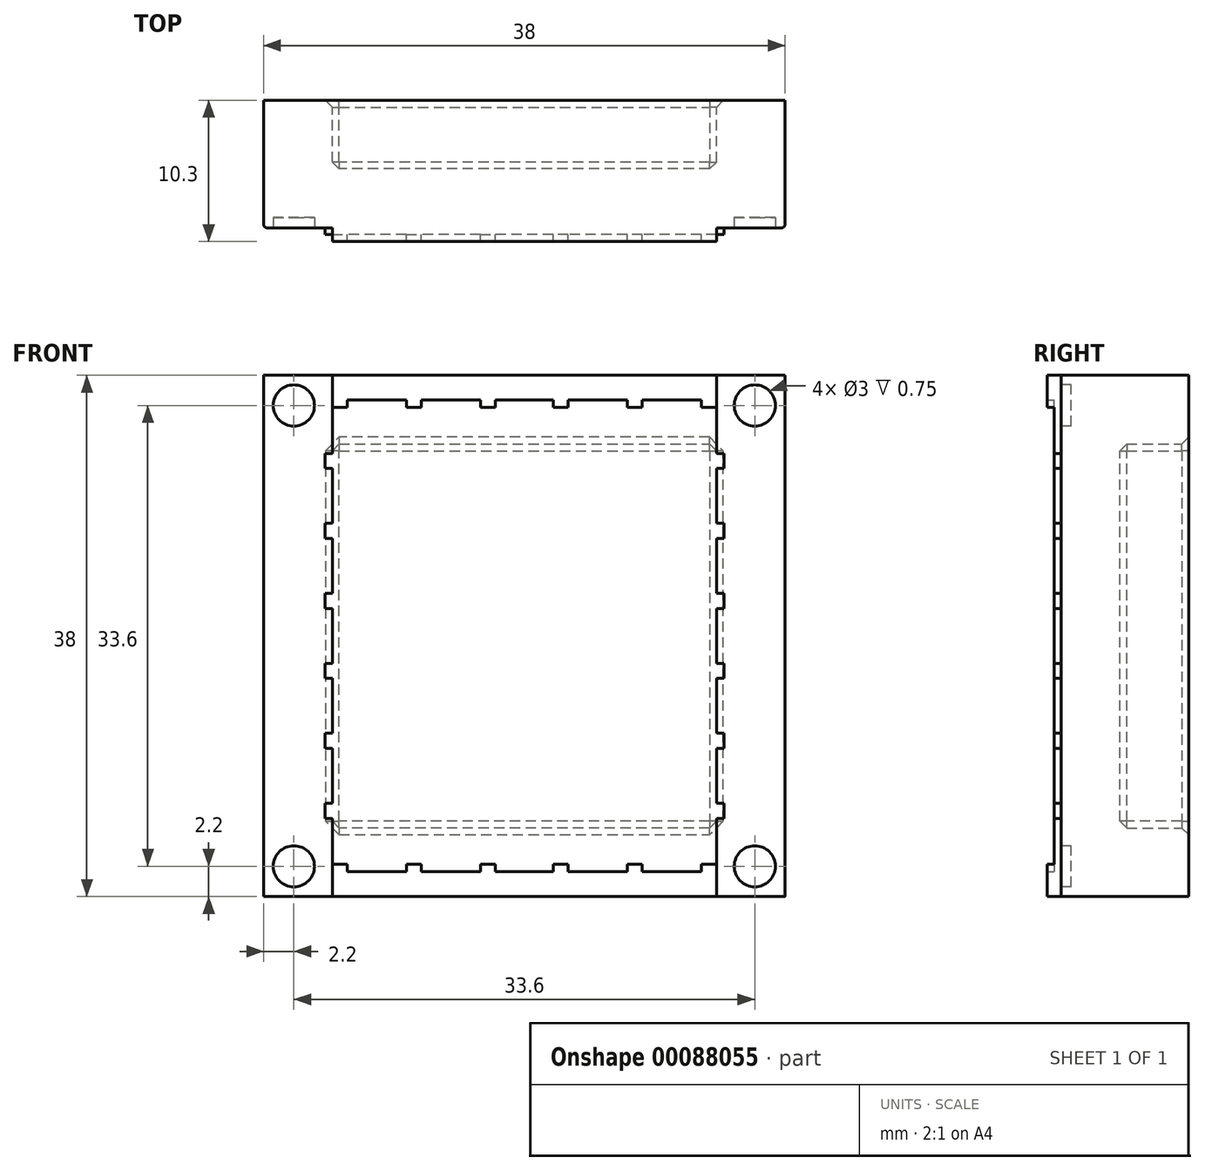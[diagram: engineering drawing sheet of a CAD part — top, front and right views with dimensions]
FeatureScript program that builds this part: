
annotation { "Feature Type Name" : "Feature", "Feature Type Description" : "" }
export const myFeature = defineFeature(function(context is Context, id is Id, definition is map)
    precondition{}
    {
        {
            var Q0;
            Q0=qCreatedBy(makeId("Front.planeOp"),FACE);
            var sketch = newSketch(context, id + "F0", { "sketchPlane" : qUnion([Q0])});
            skLineSegment(sketch, "E0.bottom", {"start": v(-19, 19) * mm, "end": v(19, 19) * mm});
            skLineSegment(sketch, "E0.top", {"start": v(-19, -19) * mm, "end": v(19, -19) * mm});
            skLineSegment(sketch, "E0.left", {"start": v(-19, 19) * mm, "end": v(-19, -19) * mm});
            skLineSegment(sketch, "E0.right", {"start": v(19, 19) * mm, "end": v(19, -19) * mm});
            skPoint(sketch, "E0.middle", {"position": v(0, 0) * mm});
            skSolve(sketch);
        }
        {
            var Q0;
            Q0 = qSketchRegion(id + "F0", true);
            extrude(context, id + "F1", {"entities" : qUnion([Q0]), "depth" : 9.3 * mm, "offsetDistance" : 25 * mm});
        }
        {
            var Q0;
            Q0=makeQuery(id+"F1.opExtrude","CAP_FACE",FACE,{"disambiguationData":[OSD([sQuery(id+"F0.wireOp",EDGE,"E0.bottom"),sQuery(id+"F0.wireOp",EDGE,"E0.top"),sQuery(id+"F0.wireOp",EDGE,"E0.left"),sQuery(id+"F0.wireOp",EDGE,"E0.right")])],"isStart":false});
            var sketch = newSketch(context, id + "F2", { "sketchPlane" : qUnion([Q0])});
            skCircle(sketch, "E1", {"center": v(-16.8, 16.8) * mm, "radius": 1.5 * mm});
            skCircle(sketch, "E2", {"center": v(16.8, 16.8) * mm, "radius": 1.5 * mm});
            skCircle(sketch, "E3", {"center": v(16.8, -16.8) * mm, "radius": 1.5 * mm});
            skCircle(sketch, "E4", {"center": v(-16.8, -16.8) * mm, "radius": 1.5 * mm});
            skSolve(sketch);
        }
        {
            var Q0;
            Q0 = qSketchRegion(id + "F2", true);
            extrude(context, id + "F3", {"entities" : qUnion([Q0]), "operationType" : NewBodyOperationType.REMOVE, "oppositeDirection" : true, "depth" : .75 * mm, "offsetDistance" : 25 * mm});
        }
        {
            var Q0;
            Q0=makeQuery(id+"F1.opExtrude","CAP_FACE",FACE,{"disambiguationData":[OSD([sQuery(id+"F0.wireOp",EDGE,"E0.bottom"),sQuery(id+"F0.wireOp",EDGE,"E0.top"),sQuery(id+"F0.wireOp",EDGE,"E0.left"),sQuery(id+"F0.wireOp",EDGE,"E0.right")])],"isStart":false});
            var sketch = newSketch(context, id + "F4", { "sketchPlane" : qUnion([Q0])});
            skLineSegment(sketch, "E5", {"start": v(0, 19) * mm, "end": v(0, -19) * mm, "construction": true});
            skLineSegment(sketch, "E6", {"start": v(0, 19) * mm, "end": v(-14, 19) * mm});
            skLineSegment(sketch, "E7", {"start": v(-14, 19) * mm, "end": v(-14, 13.3) * mm});
            skLineSegment(sketch, "E8", {"start": v(-14, 13.3) * mm, "end": v(-14.54, 13.3) * mm});
            skLineSegment(sketch, "E9", {"start": v(-14.54, 13.3) * mm, "end": v(-14.54, 12.2) * mm});
            skLineSegment(sketch, "E10", {"start": v(-14.54, 12.2) * mm, "end": v(-14, 12.2) * mm});
            skLineSegment(sketch, "E11", {"start": v(-14, 12.2) * mm, "end": v(-14, 8.2) * mm});
            skLineSegment(sketch, "E12", {"start": v(-14, 8.2) * mm, "end": v(-14.54, 8.2) * mm});
            skLineSegment(sketch, "E13", {"start": v(-14.54, 8.2) * mm, "end": v(-14.54, 7.1) * mm});
            skLineSegment(sketch, "E14", {"start": v(-14.54, 7.1) * mm, "end": v(-14, 7.1) * mm});
            skLineSegment(sketch, "E15", {"start": v(-14, 7.1) * mm, "end": v(-14, 3.1) * mm});
            skLineSegment(sketch, "E16", {"start": v(-14, 3.1) * mm, "end": v(-14.54, 3.1) * mm});
            skLineSegment(sketch, "E17", {"start": v(-14.54, 3.1) * mm, "end": v(-14.54, 2) * mm});
            skLineSegment(sketch, "E18", {"start": v(-14.54, 2) * mm, "end": v(-14, 2) * mm});
            skLineSegment(sketch, "E19", {"start": v(-14, 2) * mm, "end": v(-14, -2) * mm});
            skLineSegment(sketch, "E20", {"start": v(-14, -2) * mm, "end": v(-14.54, -2) * mm});
            skLineSegment(sketch, "E21", {"start": v(-14.54, -2) * mm, "end": v(-14.54, -3.1) * mm});
            skLineSegment(sketch, "E22", {"start": v(-14.54, -3.1) * mm, "end": v(-14, -3.1) * mm});
            skLineSegment(sketch, "E23", {"start": v(-14, -3.1) * mm, "end": v(-14, -7.1) * mm});
            skLineSegment(sketch, "E24", {"start": v(-14, -7.1) * mm, "end": v(-14.54, -7.1) * mm});
            skLineSegment(sketch, "E25", {"start": v(-14.54, -7.1) * mm, "end": v(-14.54, -8.2) * mm});
            skLineSegment(sketch, "E26", {"start": v(-14.54, -8.2) * mm, "end": v(-14, -8.2) * mm});
            skLineSegment(sketch, "E27", {"start": v(-14, -8.2) * mm, "end": v(-14, -12.2) * mm});
            skLineSegment(sketch, "E28", {"start": v(-14, -12.2) * mm, "end": v(-14.54, -12.2) * mm});
            skLineSegment(sketch, "E29", {"start": v(-14.54, -12.2) * mm, "end": v(-14.54, -13.3) * mm});
            skLineSegment(sketch, "E30", {"start": v(-14.54, -13.3) * mm, "end": v(-14, -13.3) * mm});
            skLineSegment(sketch, "E31", {"start": v(-14, -13.3) * mm, "end": v(-14, -19) * mm});
            skLineSegment(sketch, "E32", {"start": v(-14, -19) * mm, "end": v(0, -19) * mm});
            skLineSegment(sketch, "E33.MirrorCS", {"start": v(14, 8.2) * mm, "end": v(14.54, 8.2) * mm});
            skLineSegment(sketch, "E34.MirrorCS", {"start": v(14.54, 13.3) * mm, "end": v(14.54, 12.2) * mm});
            skLineSegment(sketch, "E35.MirrorCS", {"start": v(14, -8.2) * mm, "end": v(14, -12.2) * mm});
            skLineSegment(sketch, "E36.MirrorCS", {"start": v(14.54, -2) * mm, "end": v(14.54, -3.1) * mm});
            skLineSegment(sketch, "E37.MirrorCS", {"start": v(14, -12.2) * mm, "end": v(14.54, -12.2) * mm});
            skLineSegment(sketch, "E38.MirrorCS", {"start": v(14.54, -13.3) * mm, "end": v(14, -13.3) * mm});
            skLineSegment(sketch, "E39.MirrorCS", {"start": v(14, -2) * mm, "end": v(14.54, -2) * mm});
            skLineSegment(sketch, "E40.MirrorCS", {"start": v(14.54, 7.1) * mm, "end": v(14, 7.1) * mm});
            skLineSegment(sketch, "E41.MirrorCS", {"start": v(14.54, -3.1) * mm, "end": v(14, -3.1) * mm});
            skLineSegment(sketch, "E42.MirrorCS", {"start": v(14, 3.1) * mm, "end": v(14.54, 3.1) * mm});
            skLineSegment(sketch, "E43.MirrorCS", {"start": v(14, 13.3) * mm, "end": v(14.54, 13.3) * mm});
            skLineSegment(sketch, "E44.MirrorCS", {"start": v(14.54, 2) * mm, "end": v(14, 2) * mm});
            skLineSegment(sketch, "E45.MirrorCS", {"start": v(14.54, -8.2) * mm, "end": v(14, -8.2) * mm});
            skLineSegment(sketch, "E46.MirrorCS", {"start": v(14, -13.3) * mm, "end": v(14, -19) * mm});
            skLineSegment(sketch, "E47.MirrorCS", {"start": v(14, -7.1) * mm, "end": v(14.54, -7.1) * mm});
            skLineSegment(sketch, "E48.MirrorCS", {"start": v(14.54, -12.2) * mm, "end": v(14.54, -13.3) * mm});
            skLineSegment(sketch, "E49.MirrorCS", {"start": v(14.54, 12.2) * mm, "end": v(14, 12.2) * mm});
            skLineSegment(sketch, "E50.MirrorCS", {"start": v(0, 19) * mm, "end": v(14, 19) * mm});
            skLineSegment(sketch, "E51.MirrorCS", {"start": v(14.54, 8.2) * mm, "end": v(14.54, 7.1) * mm});
            skLineSegment(sketch, "E52.MirrorCS", {"start": v(14, -19) * mm, "end": v(0, -19) * mm});
            skLineSegment(sketch, "E53.MirrorCS", {"start": v(14, 19) * mm, "end": v(14, 13.3) * mm});
            skLineSegment(sketch, "E54.MirrorCS", {"start": v(14, 12.2) * mm, "end": v(14, 8.2) * mm});
            skLineSegment(sketch, "E55.MirrorCS", {"start": v(14.54, -7.1) * mm, "end": v(14.54, -8.2) * mm});
            skLineSegment(sketch, "E56.MirrorCS", {"start": v(14, 2) * mm, "end": v(14, -2) * mm});
            skLineSegment(sketch, "E57.MirrorCS", {"start": v(14, -3.1) * mm, "end": v(14, -7.1) * mm});
            skLineSegment(sketch, "E58.MirrorCS", {"start": v(14.54, 3.1) * mm, "end": v(14.54, 2) * mm});
            skLineSegment(sketch, "E59.MirrorCS", {"start": v(14, 7.1) * mm, "end": v(14, 3.1) * mm});
            skSolve(sketch);
        }
        {
            var Q0;
            Q0 = qSketchRegion(id + "F4", true);
            extrude(context, id + "F5", {"entities" : qUnion([Q0]), "operationType" : NewBodyOperationType.ADD, "depth" : .5 * mm, "offsetDistance" : 25 * mm});
        }
        {
            var Q0;
            Q0=makeQuery(id+"F5.opExtrude","CAP_FACE",FACE,{"disambiguationData":[OSD([sQuery(id+"F4.wireOp",EDGE,"E6"),sQuery(id+"F4.wireOp",EDGE,"E7"),sQuery(id+"F4.wireOp",EDGE,"E8"),sQuery(id+"F4.wireOp",EDGE,"E9"),sQuery(id+"F4.wireOp",EDGE,"E10"),sQuery(id+"F4.wireOp",EDGE,"E11"),sQuery(id+"F4.wireOp",EDGE,"E12"),sQuery(id+"F4.wireOp",EDGE,"E13"),sQuery(id+"F4.wireOp",EDGE,"E14"),sQuery(id+"F4.wireOp",EDGE,"E15"),sQuery(id+"F4.wireOp",EDGE,"E16"),sQuery(id+"F4.wireOp",EDGE,"E17"),sQuery(id+"F4.wireOp",EDGE,"E18"),sQuery(id+"F4.wireOp",EDGE,"E19"),sQuery(id+"F4.wireOp",EDGE,"E20"),sQuery(id+"F4.wireOp",EDGE,"E21"),sQuery(id+"F4.wireOp",EDGE,"E22"),sQuery(id+"F4.wireOp",EDGE,"E23"),sQuery(id+"F4.wireOp",EDGE,"E24"),sQuery(id+"F4.wireOp",EDGE,"E25"),sQuery(id+"F4.wireOp",EDGE,"E26"),sQuery(id+"F4.wireOp",EDGE,"E27"),sQuery(id+"F4.wireOp",EDGE,"E28"),sQuery(id+"F4.wireOp",EDGE,"E29"),sQuery(id+"F4.wireOp",EDGE,"E30"),sQuery(id+"F4.wireOp",EDGE,"E31"),sQuery(id+"F4.wireOp",EDGE,"E32"),sQuery(id+"F4.wireOp",EDGE,"E33.MirrorCS"),sQuery(id+"F4.wireOp",EDGE,"E34.MirrorCS"),sQuery(id+"F4.wireOp",EDGE,"E35.MirrorCS"),sQuery(id+"F4.wireOp",EDGE,"E36.MirrorCS"),sQuery(id+"F4.wireOp",EDGE,"E37.MirrorCS"),sQuery(id+"F4.wireOp",EDGE,"E38.MirrorCS"),sQuery(id+"F4.wireOp",EDGE,"E39.MirrorCS"),sQuery(id+"F4.wireOp",EDGE,"E40.MirrorCS"),sQuery(id+"F4.wireOp",EDGE,"E41.MirrorCS"),sQuery(id+"F4.wireOp",EDGE,"E42.MirrorCS"),sQuery(id+"F4.wireOp",EDGE,"E43.MirrorCS"),sQuery(id+"F4.wireOp",EDGE,"E44.MirrorCS"),sQuery(id+"F4.wireOp",EDGE,"E45.MirrorCS"),sQuery(id+"F4.wireOp",EDGE,"E46.MirrorCS"),sQuery(id+"F4.wireOp",EDGE,"E47.MirrorCS"),sQuery(id+"F4.wireOp",EDGE,"E48.MirrorCS"),sQuery(id+"F4.wireOp",EDGE,"E49.MirrorCS"),sQuery(id+"F4.wireOp",EDGE,"E50.MirrorCS"),sQuery(id+"F4.wireOp",EDGE,"E51.MirrorCS"),sQuery(id+"F4.wireOp",EDGE,"E52.MirrorCS"),sQuery(id+"F4.wireOp",EDGE,"E53.MirrorCS"),sQuery(id+"F4.wireOp",EDGE,"E54.MirrorCS"),sQuery(id+"F4.wireOp",EDGE,"E55.MirrorCS"),sQuery(id+"F4.wireOp",EDGE,"E56.MirrorCS"),sQuery(id+"F4.wireOp",EDGE,"E57.MirrorCS"),sQuery(id+"F4.wireOp",EDGE,"E58.MirrorCS"),sQuery(id+"F4.wireOp",EDGE,"E59.MirrorCS")])],"isStart":false});
            var sketch = newSketch(context, id + "F6", { "sketchPlane" : qUnion([Q0])});
            skLineSegment(sketch, "E60.bottom", {"start": v(14, 19) * mm, "end": v(-14, 19) * mm});
            skLineSegment(sketch, "E60.top", {"start": v(14, 17.2) * mm, "end": v(-14, 17.2) * mm});
            skLineSegment(sketch, "E60.left", {"start": v(14, 19) * mm, "end": v(14, 17.2) * mm});
            skLineSegment(sketch, "E60.right", {"start": v(-14, 19) * mm, "end": v(-14, 17.2) * mm});
            skLineSegment(sketch, "E61", {"start": v(0, 0) * mm, "end": v(19.52, 0) * mm, "construction": true});
            skLineSegment(sketch, "E62", {"start": v(-14, 17.2) * mm, "end": v(-14, 16.66) * mm});
            skLineSegment(sketch, "E63", {"start": v(-14, 16.66) * mm, "end": v(-12.9, 16.66) * mm});
            skLineSegment(sketch, "E64", {"start": v(-12.9, 16.66) * mm, "end": v(-12.9, 17.2) * mm});
            skLineSegment(sketch, "E65", {"start": v(14, 17.2) * mm, "end": v(14, 16.66) * mm});
            skLineSegment(sketch, "E66", {"start": v(14, 16.66) * mm, "end": v(12.9, 16.66) * mm});
            skLineSegment(sketch, "E67", {"start": v(12.9, 16.66) * mm, "end": v(12.9, 17.2) * mm});
            skLineSegment(sketch, "E68", {"start": v(-8.6, 17.2) * mm, "end": v(-8.6, 16.66) * mm});
            skLineSegment(sketch, "E69", {"start": v(-8.6, 16.66) * mm, "end": v(-7.5, 16.66) * mm});
            skLineSegment(sketch, "E70", {"start": v(-7.5, 16.66) * mm, "end": v(-7.5, 17.2) * mm});
            skLineSegment(sketch, "E71", {"start": v(-3.2, 17.2) * mm, "end": v(-3.2, 16.66) * mm});
            skLineSegment(sketch, "E72", {"start": v(-3.2, 16.66) * mm, "end": v(-2.1, 16.66) * mm});
            skLineSegment(sketch, "E73", {"start": v(-2.1, 16.66) * mm, "end": v(-2.1, 17.2) * mm});
            skLineSegment(sketch, "E74", {"start": v(8.6, 17.2) * mm, "end": v(8.6, 16.66) * mm});
            skLineSegment(sketch, "E75", {"start": v(8.6, 16.66) * mm, "end": v(7.5, 16.66) * mm});
            skLineSegment(sketch, "E76", {"start": v(7.5, 16.66) * mm, "end": v(7.5, 17.2) * mm});
            skLineSegment(sketch, "E77", {"start": v(3.2, 17.2) * mm, "end": v(3.2, 16.66) * mm});
            skLineSegment(sketch, "E78", {"start": v(3.2, 16.66) * mm, "end": v(2.1, 16.66) * mm});
            skLineSegment(sketch, "E79", {"start": v(2.1, 16.66) * mm, "end": v(2.1, 17.2) * mm});
            skLineSegment(sketch, "E80.MirrorCS", {"start": v(-14, -16.66) * mm, "end": v(-12.9, -16.66) * mm});
            skLineSegment(sketch, "E81.MirrorCS", {"start": v(14, -16.66) * mm, "end": v(12.9, -16.66) * mm});
            skLineSegment(sketch, "E82.MirrorCS", {"start": v(-3.2, -17.2) * mm, "end": v(-3.2, -16.66) * mm});
            skLineSegment(sketch, "E83.MirrorCS", {"start": v(8.6, -17.2) * mm, "end": v(8.6, -16.66) * mm});
            skLineSegment(sketch, "E84.MirrorCS", {"start": v(2.1, -16.66) * mm, "end": v(2.1, -17.2) * mm});
            skLineSegment(sketch, "E85.MirrorCS", {"start": v(12.9, -16.66) * mm, "end": v(12.9, -17.2) * mm});
            skLineSegment(sketch, "E86.MirrorCS", {"start": v(-3.2, -16.66) * mm, "end": v(-2.1, -16.66) * mm});
            skLineSegment(sketch, "E87.MirrorCS", {"start": v(-2.1, -16.66) * mm, "end": v(-2.1, -17.2) * mm});
            skLineSegment(sketch, "E88.MirrorCS", {"start": v(3.2, -16.66) * mm, "end": v(2.1, -16.66) * mm});
            skLineSegment(sketch, "E89.MirrorCS", {"start": v(-7.5, -16.66) * mm, "end": v(-7.5, -17.2) * mm});
            skLineSegment(sketch, "E90.MirrorCS", {"start": v(3.2, -17.2) * mm, "end": v(3.2, -16.66) * mm});
            skLineSegment(sketch, "E91.MirrorCS", {"start": v(8.6, -16.66) * mm, "end": v(7.5, -16.66) * mm});
            skLineSegment(sketch, "E92.MirrorCS", {"start": v(7.5, -16.66) * mm, "end": v(7.5, -17.2) * mm});
            skLineSegment(sketch, "E93.MirrorCS", {"start": v(-12.9, -16.66) * mm, "end": v(-12.9, -17.2) * mm});
            skLineSegment(sketch, "E94.MirrorCS", {"start": v(-8.6, -17.2) * mm, "end": v(-8.6, -16.66) * mm});
            skLineSegment(sketch, "E95.MirrorCS", {"start": v(14, -17.2) * mm, "end": v(14, -16.66) * mm});
            skLineSegment(sketch, "E96.MirrorCS", {"start": v(-8.6, -16.66) * mm, "end": v(-7.5, -16.66) * mm});
            skLineSegment(sketch, "E97.MirrorCS", {"start": v(-14, -17.2) * mm, "end": v(-14, -16.66) * mm});
            skLineSegment(sketch, "E98.MirrorCS", {"start": v(14, -19) * mm, "end": v(14, -17.2) * mm});
            skLineSegment(sketch, "E99.MirrorCS", {"start": v(-14, -19) * mm, "end": v(-14, -17.2) * mm});
            skLineSegment(sketch, "E100.MirrorCS", {"start": v(14, -19) * mm, "end": v(-14, -19) * mm});
            skLineSegment(sketch, "E101.MirrorCS", {"start": v(14, -17.2) * mm, "end": v(-14, -17.2) * mm});
            skSolve(sketch);
        }
        {
            var Q0;
            Q0 = qSketchRegion(id + "F6", true);
            extrude(context, id + "F7", {"entities" : qUnion([Q0]), "operationType" : NewBodyOperationType.ADD, "depth" : .5 * mm, "offsetDistance" : 25 * mm});
        }
        {
            var Q0;
            Q0=makeQuery(id+"F1.opExtrude","CAP_EDGE",EDGE,{"disambiguationData":[OSD([sQuery(id+"F0.wireOp",EDGE,"E0.left")])],"isStart":false});
            var Q1;
            Q1=makeQuery(id+"F1.opExtrude","CAP_EDGE",EDGE,{"disambiguationData":[OSD([sQuery(id+"F0.wireOp",EDGE,"E0.right")])],"isStart":false});
            fillet(context, id + "F8", {"entities" : qUnion([Q0, Q1]), "radius" : .25 * mm, "tangentPropagation" : true, "allowEdgeOverflow" : false});
        }
        {
            var Q0;
            Q0=makeQuery(id+"F0.imprint","IMPRINT",FACE,{"disambiguationData":[TD([[makeQuery(id+"F0.imprint","IMPRINT",EDGE,{"derivedFrom":sQuery(id+"F0.wireOp",EDGE,"E0.bottom")}),-1.0]])]});
            var sketch = newSketch(context, id + "F9", { "sketchPlane" : qUnion([Q0])});
            skLineSegment(sketch, "E102.bottom", {"start": v(14, 14) * mm, "end": v(-14, 14) * mm});
            skLineSegment(sketch, "E102.top", {"start": v(14, -14) * mm, "end": v(-14, -14) * mm});
            skLineSegment(sketch, "E102.left", {"start": v(14, 14) * mm, "end": v(14, -14) * mm});
            skLineSegment(sketch, "E102.right", {"start": v(-14, 14) * mm, "end": v(-14, -14) * mm});
            skPoint(sketch, "E102.middle", {"position": v(0, 0) * mm});
            skSolve(sketch);
        }
        {
            var Q0;
            Q0 = qSketchRegion(id + "F9", true);
            extrude(context, id + "F10", {"entities" : qUnion([Q0]), "operationType" : NewBodyOperationType.REMOVE, "depth" : 5 * mm, "offsetDistance" : 25 * mm});
        }
        {
            var Q0;
            Q0=makeQuery(id+"F10.boolean.opBoolean","COPY",EDGE,{"derivedFrom":makeQuery(id+"F10.opExtrude","SWEPT_EDGE",EDGE,{"disambiguationData":[OSD([sQuery(id+"F9.wireOp",EDGE,"E102.bottom"),sQuery(id+"F9.wireOp",EDGE,"E102.right")])]})});
            var Q1;
            Q1=makeQuery(id+"F10.boolean.opBoolean","COPY",EDGE,{"derivedFrom":makeQuery(id+"F10.opExtrude","CAP_EDGE",EDGE,{"disambiguationData":[OSD([sQuery(id+"F9.wireOp",EDGE,"E102.bottom")])],"isStart":false})});
            var Q2;
            Q2=makeQuery(id+"F10.boolean.opBoolean","COPY",EDGE,{"derivedFrom":makeQuery(id+"F10.opExtrude","CAP_EDGE",EDGE,{"disambiguationData":[OSD([sQuery(id+"F9.wireOp",EDGE,"E102.right")])],"isStart":false})});
            var Q3;
            Q3=makeQuery(id+"F10.boolean.opBoolean","COPY",EDGE,{"derivedFrom":makeQuery(id+"F10.opExtrude","SWEPT_EDGE",EDGE,{"disambiguationData":[OSD([sQuery(id+"F9.wireOp",EDGE,"E102.bottom"),sQuery(id+"F9.wireOp",EDGE,"E102.left")])]})});
            var Q4;
            Q4=makeQuery(id+"F10.boolean.opBoolean","COPY",FACE,{"derivedFrom":makeQuery(id+"F10.opExtrude","SWEPT_FACE",FACE,{"disambiguationData":[OSD([sQuery(id+"F9.wireOp",EDGE,"E102.left")])]})});
            var Q5;
            Q5=makeQuery(id+"F10.boolean.opBoolean","COPY",FACE,{"derivedFrom":makeQuery(id+"F10.opExtrude","SWEPT_FACE",FACE,{"disambiguationData":[OSD([sQuery(id+"F9.wireOp",EDGE,"E102.top")])]})});
            chamfer(context, id + "F11", {"entities" : qUnion([Q0, Q1, Q2, Q3, Q4, Q5]), "width" : .5 * mm, "tangentPropagation" : true});
        }
    });
